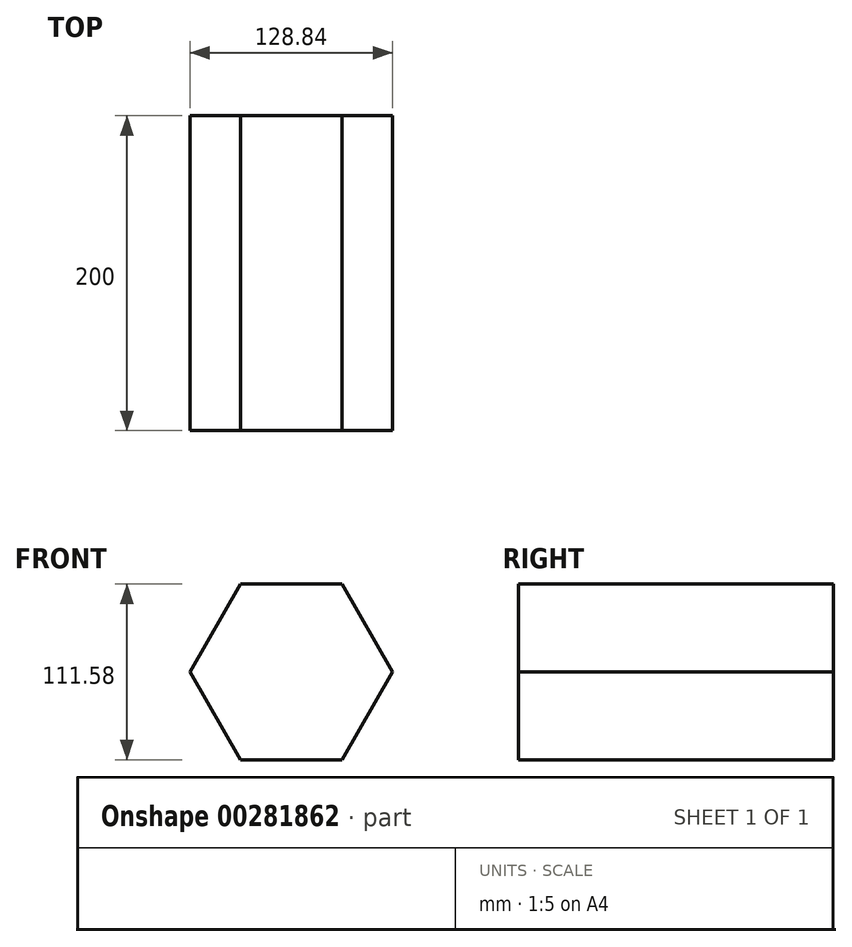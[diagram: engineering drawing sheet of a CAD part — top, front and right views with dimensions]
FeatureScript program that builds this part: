
annotation { "Feature Type Name" : "Feature", "Feature Type Description" : "" }
export const myFeature = defineFeature(function(context is Context, id is Id, definition is map)
    precondition{}
    {
        {
            var Q0;
            Q0=qCreatedBy(makeId("Front.planeOp"),FACE);
            var sketch = newSketch(context, id + "F0", { "sketchPlane" : qUnion([Q0])});
            skCircle(sketch, "E0.cCircle", {"center": v(0, 0) * mm, "radius": 64.42 * mm, "construction": true});
            skLineSegment(sketch, "E0.0", {"start": v(64.42, 0) * mm, "end": v(32.2, -55.79) * mm});
            skLineSegment(sketch, "E0.1", {"start": v(32.2, -55.79) * mm, "end": v(-32.2, -55.79) * mm});
            skLineSegment(sketch, "E0.2", {"start": v(-32.2, -55.79) * mm, "end": v(-64.42, 0) * mm});
            skLineSegment(sketch, "E0.3", {"start": v(-64.42, 0) * mm, "end": v(-32.2, 55.79) * mm});
            skLineSegment(sketch, "E0.4", {"start": v(-32.2, 55.79) * mm, "end": v(32.2, 55.79) * mm});
            skLineSegment(sketch, "E0.5", {"start": v(32.2, 55.79) * mm, "end": v(64.42, 0) * mm});
            skSolve(sketch);
        }
        {
            var Q0;
            Q0=makeQuery(id+"F0.imprint","IMPRINT",FACE,{"disambiguationData":[TD([[makeQuery(id+"F0.imprint","IMPRINT",EDGE,{"derivedFrom":sQuery(id+"F0.wireOp",EDGE,"E0.0")}),-1.0]])]});
            extrude(context, id + "F1", {"entities" : qUnion([Q0]), "depth" : 200 * mm});
        }
    });
